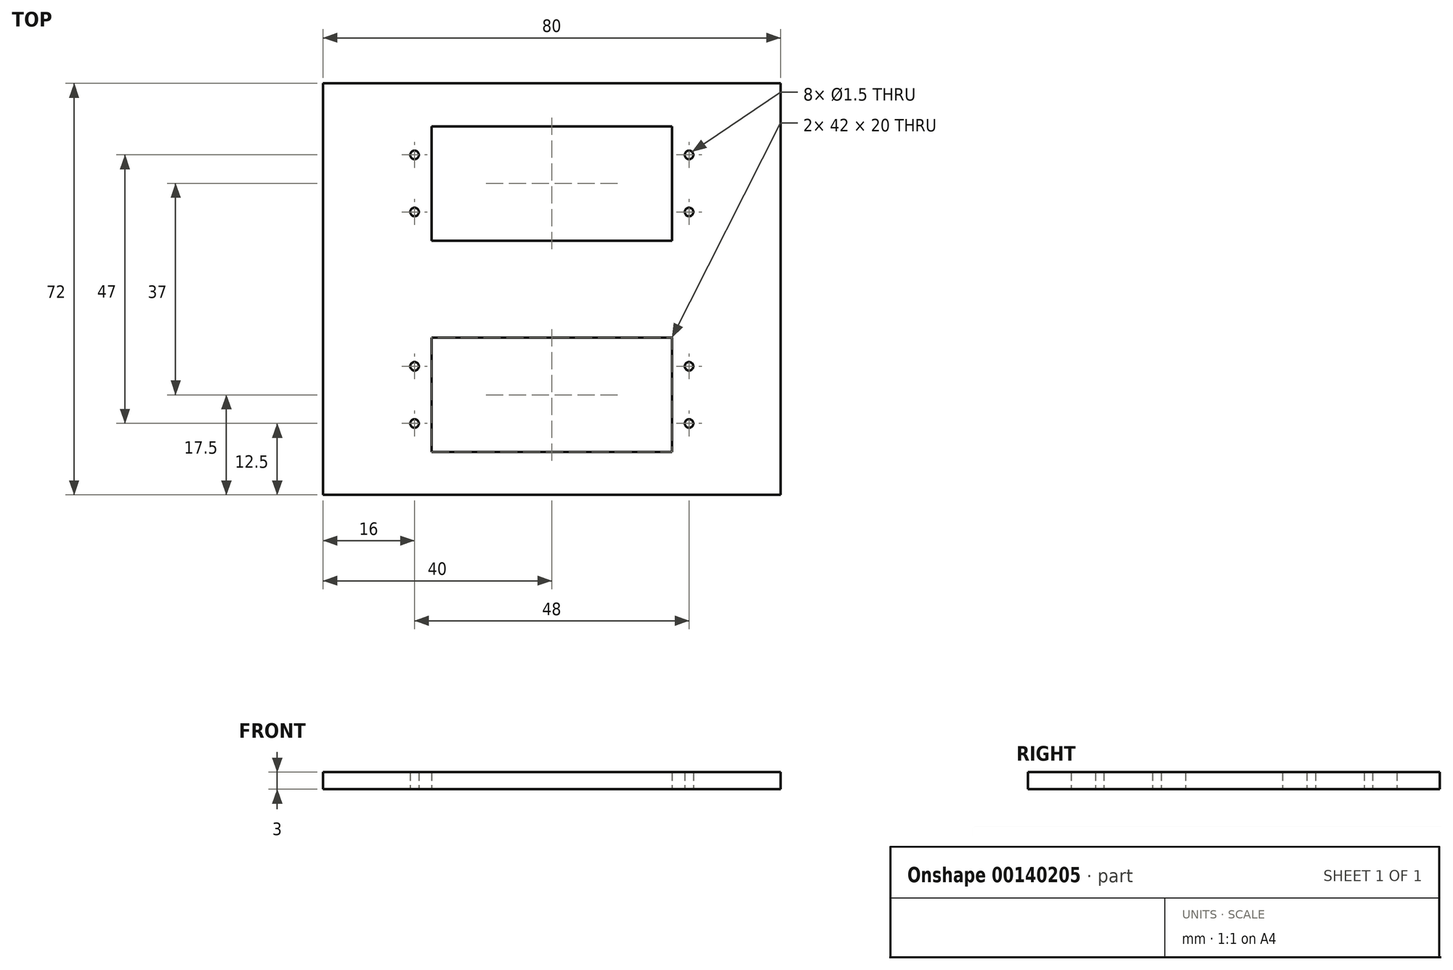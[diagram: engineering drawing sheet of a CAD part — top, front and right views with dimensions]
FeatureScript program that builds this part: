
annotation { "Feature Type Name" : "Feature", "Feature Type Description" : "" }
export const myFeature = defineFeature(function(context is Context, id is Id, definition is map)
    precondition{}
    {
        {
            var Q0;
            Q0=qCreatedBy(makeId("Top.planeOp"),FACE);
            var sketch = newSketch(context, id + "F0", { "sketchPlane" : qUnion([Q0])});
            skLineSegment(sketch, "E0.bottom", {"start": v(-40, 36) * mm, "end": v(40, 36) * mm});
            skLineSegment(sketch, "E0.top", {"start": v(-40, -36) * mm, "end": v(40, -36) * mm});
            skLineSegment(sketch, "E0.left", {"start": v(-40, 36) * mm, "end": v(-40, -36) * mm});
            skLineSegment(sketch, "E0.right", {"start": v(40, 36) * mm, "end": v(40, -36) * mm});
            skPoint(sketch, "E1", {"position": v(0, 36) * mm});
            skPoint(sketch, "E2", {"position": v(40, 0) * mm});
            skLineSegment(sketch, "E3.bottom", {"start": v(-21, 28.5) * mm, "end": v(21, 28.5) * mm});
            skLineSegment(sketch, "E3.top", {"start": v(-21, 8.5) * mm, "end": v(21, 8.5) * mm});
            skLineSegment(sketch, "E3.left", {"start": v(-21, 28.5) * mm, "end": v(-21, 8.5) * mm});
            skLineSegment(sketch, "E3.right", {"start": v(21, 28.5) * mm, "end": v(21, 8.5) * mm});
            skPoint(sketch, "E4", {"position": v(0, 28.5) * mm});
            skLineSegment(sketch, "E5", {"start": v(-54.38, 18.5) * mm, "end": v(18.35, 18.5) * mm, "construction": true});
            skPoint(sketch, "E6", {"position": v(-29.55, 18.5) * mm});
            skPoint(sketch, "E7", {"position": v(-21, 18.5) * mm});
            skCircle(sketch, "E8", {"center": v(-24, 23.5) * mm, "radius": 0.75 * mm});
            skCircle(sketch, "E9.MirrorC", {"center": v(24, 23.5) * mm, "radius": 0.75 * mm});
            skLineSegment(sketch, "E10.MirrorCS", {"start": v(54.38, 18.5) * mm, "end": v(-18.35, 18.5) * mm, "construction": true});
            skCircle(sketch, "E11.MirrorC", {"center": v(-24, 13.5) * mm, "radius": 0.75 * mm});
            skCircle(sketch, "E12.MirrorC", {"center": v(24, 13.5) * mm, "radius": 0.75 * mm});
            skLineSegment(sketch, "E13.MirrorCS", {"start": v(-21, -8.5) * mm, "end": v(21, -8.5) * mm});
            skLineSegment(sketch, "E14.MirrorCS", {"start": v(-21, -28.5) * mm, "end": v(-21, -8.5) * mm});
            skLineSegment(sketch, "E15.MirrorCS", {"start": v(-21, -28.5) * mm, "end": v(21, -28.5) * mm});
            skLineSegment(sketch, "E16.MirrorCS", {"start": v(21, -28.5) * mm, "end": v(21, -8.5) * mm});
            skCircle(sketch, "E17.MirrorC", {"center": v(24, -13.5) * mm, "radius": 0.75 * mm});
            skCircle(sketch, "E18.MirrorC", {"center": v(24, -23.5) * mm, "radius": 0.75 * mm});
            skCircle(sketch, "E19.MirrorC", {"center": v(-24, -23.5) * mm, "radius": 0.75 * mm});
            skCircle(sketch, "E20.MirrorC", {"center": v(-24, -13.5) * mm, "radius": 0.75 * mm});
            skSolve(sketch);
        }
        {
            var Q0;
            Q0=makeQuery(id+"F0.imprint","IMPRINT",FACE,{"disambiguationData":[TD([[makeQuery(id+"F0.imprint","IMPRINT",EDGE,{"derivedFrom":sQuery(id+"F0.wireOp",EDGE,"E0.bottom")}),-1.0]])]});
            extrude(context, id + "F1", {"entities" : qUnion([Q0]), "depth" : 3 * mm});
        }
    });
